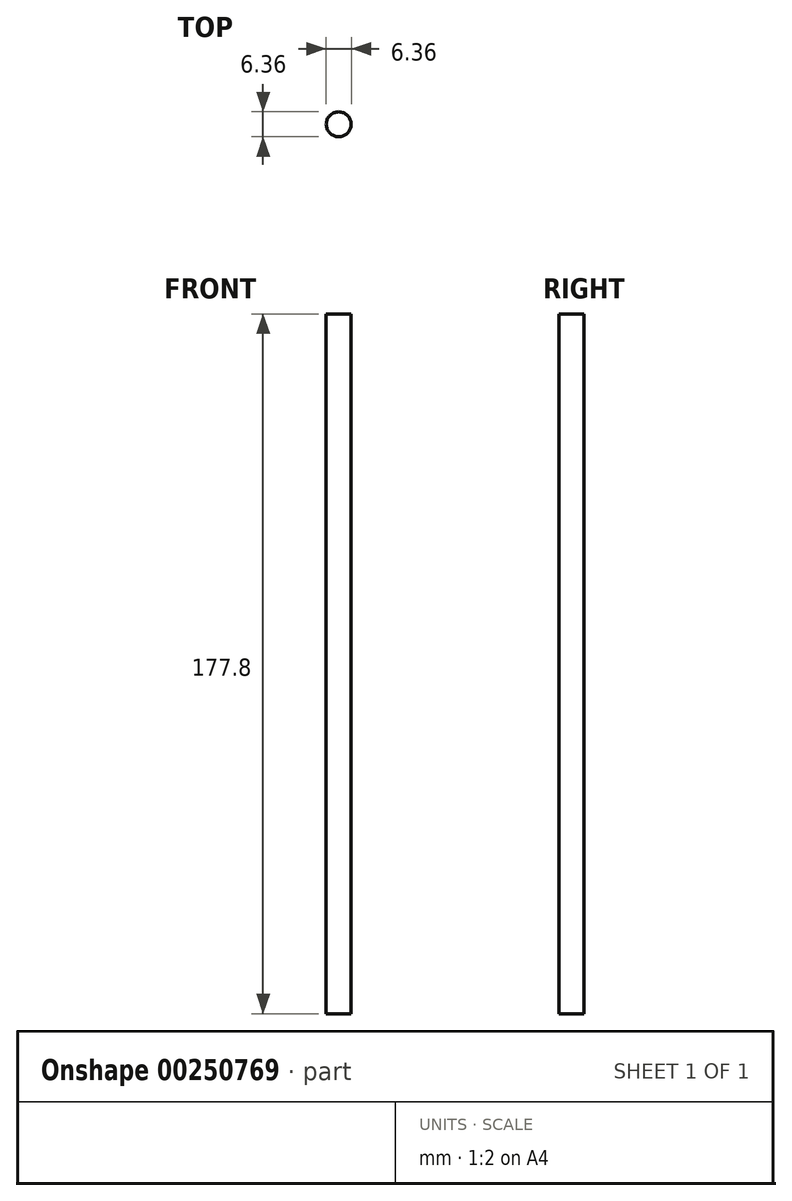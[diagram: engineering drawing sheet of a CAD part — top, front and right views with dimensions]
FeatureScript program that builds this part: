
annotation { "Feature Type Name" : "Feature", "Feature Type Description" : "" }
export const myFeature = defineFeature(function(context is Context, id is Id, definition is map)
    precondition{}
    {
        {
            var Q0;
            Q0=qCreatedBy(makeId("Top.planeOp"),FACE);
            var sketch = newSketch(context, id + "F0", { "sketchPlane" : qUnion([Q0])});
            skCircle(sketch, "E0", {"center": v(0, 0) * mm, "radius": 3.18 * mm});
            skSolve(sketch);
        }
        {
            var Q0;
            Q0=makeQuery(id+"F0.imprint","IMPRINT",FACE,{"disambiguationData":[TD([[makeQuery(id+"F0.imprint","IMPRINT",EDGE,{"derivedFrom":sQuery(id+"F0.wireOp",EDGE,"E0")}),1.0]])]});
            extrude(context, id + "F1", {"entities" : qUnion([Q0]), "depth" : 177.8 * mm});
        }
    });
